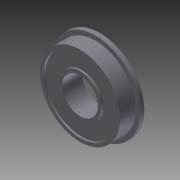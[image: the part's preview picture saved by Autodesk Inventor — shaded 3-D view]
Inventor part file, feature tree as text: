
AUTODESK INVENTOR PART (.ipt)
format: ipt  version: 2012 (Build 160160000, 160)  size: 115,200 bytes
history: native  units: in
note: dims shown in document units (in); Inventor stores cm internally (conversion verified against a paired STEP export)
features: extrude x4, sketch x2
ambient origin geometry x8: Origin, YZ Plane, XZ Plane, XY Plane, X Axis, Y Axis, Z Axis, Center Point
bodies: Solid1 (feature_tree)
feature tree (6):
  sketch  "Sketch1"  dims[d0=0.5in d1=1.125in]
  extrude  "Extrusion1"  Depth=1.125in
  extrude  "Extrusion2"  Depth=0.28in TaperAngle=0.0deg
  extrude  "Extrusion3"  Depth=0.062in TaperAngle=0.0deg
  extrude  "Extrusion4"  Depth=0.6in
  sketch  "Sketch2"  dims[d2=1.249in d3=0.28in d4=0.0in d5=0.062in d6=0.0in d7=0.6in d8=1.025in d9=0.025in d10=0.0in d11=0.025in d12=0.0in]
